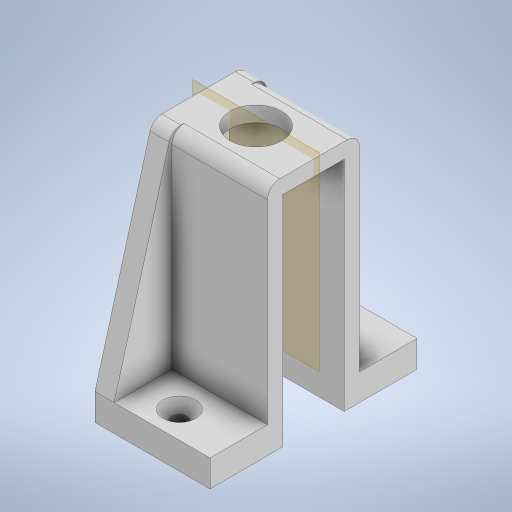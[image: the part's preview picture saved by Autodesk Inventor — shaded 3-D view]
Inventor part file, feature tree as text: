
AUTODESK INVENTOR PART (.ipt)
format: ipt  version: 2024 (Build 280153020, 153B)  size: 321,024 bytes
history: native  units: in
note: dims shown in document units (in); Inventor stores cm internally (conversion verified against a paired STEP export)
features: sketch x7, extrude x6, plane x1, hole x1, mirror x1, fillet x1, projected_geometry x1
ambient origin geometry x8: Origin, YZ Plane, XZ Plane, XY Plane, X Axis, Y Axis, Z Axis, Center Point
bodies: Body1 (feature_tree)
feature tree (18):
  extrude  "Extrusion2"  Depth=0.9449in
  extrude  "Extrusion3"  Depth=0.1575in
  extrude  "Extrusion4"  Depth=2.126in TaperAngle=0.0deg
  plane  "Work Plane1"
  extrude  "Extrusion5"  Depth=0.5906in TaperAngle=0.0deg
  hole  "Hole1"  [1 undecoded]
  extrude  "Extrusion6"  Depth=0.1969in TaperAngle=0.0deg
  mirror  "Mirror1"
  fillet  "Fillet2"  Radius=0.125in
  extrude  "Extrusion7"  Depth=0.125in TaperAngle=0.0deg
  sketch  "Sketch2"  dims[d5=1.1811in d6=0.9449in]
  sketch  "Sketch3"  dims[d7=0.1575in d8=0.0in d9=0.1575in]
  sketch  "Sketch4"  dims[d10=0.1575in d11=2.126in d12=0.0in]
  sketch  "Sketch5"  dims[d13=0.1575in d14=0.5906in d15=0.0in]
  sketch  "Sketch6"  dims[d16=0.53in d17=0.5969in d18=0.0in]
  sketch  "Sketch7"  dims[d19=0.2756in]
  sketch  "Sketch8"  dims[d20=0.1575in d21=0.75in d22=0.3346in d23=0.25in d24=0.5635in d25=1.0in d26=0.8108in d27=0.1969in d28=0.0in d29=0.125in d30=0.1181in d31=0.0in d32=0.5in d33=0.0344in]
  projected_geometry  "Projected Loop1"
note: 1 required parameter value undecoded (feature->parameter linkage not recoverable at this tier; creation-order binding heuristic only, values carry confidence <= 0.55)
